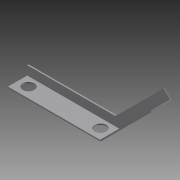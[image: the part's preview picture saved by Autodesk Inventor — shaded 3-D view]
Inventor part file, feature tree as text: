
AUTODESK INVENTOR PART (.ipt)
format: ipt  version: 2012 (Build 160160000, 160)  size: 107,520 bytes
history: native  units: in
note: dims shown in document units (in); Inventor stores cm internally (conversion verified against a paired STEP export)
features: extrude x3, sketch x2
ambient origin geometry x8: Origin, YZ Plane, XZ Plane, XY Plane, X Axis, Y Axis, Z Axis, Center Point
bodies: Solid1 (feature_tree)
feature tree (5):
  sketch  "Sketch1"  dims[d4=0.125in d6=0.125in]
  extrude  "Extrusion1"  Depth=0.125in
  extrude  "Extrusion2"  Depth=1.0in
  extrude  "Extrusion3"  TaperAngle=45.0deg  [1 undecoded]
  sketch  "Sketch2"  dims[d8=1.0in d9=1.0in d10=45.0deg d11=9.0in d12=7.0in d13=0.0625in d14=0.125in d15=0.0in d16=2.0in d17=0.0in d18=1.125in d19=1.0in d20=1.0in d21=1.0in d22=1.0in d23=0.0in]
note: 1 required parameter value undecoded (feature->parameter linkage not recoverable at this tier; creation-order binding heuristic only, values carry confidence <= 0.55)
